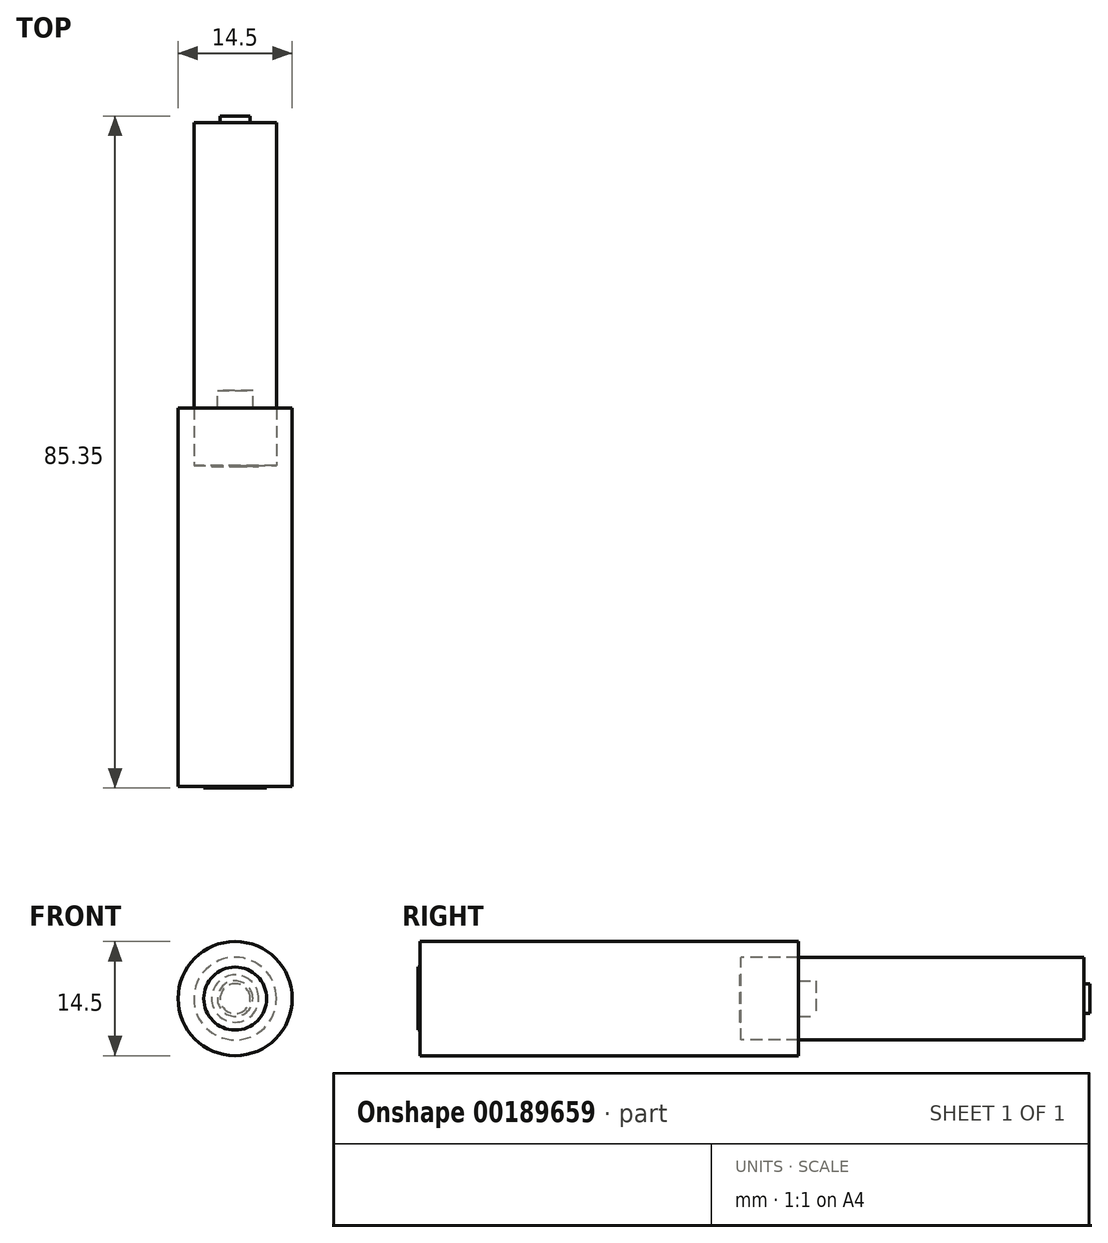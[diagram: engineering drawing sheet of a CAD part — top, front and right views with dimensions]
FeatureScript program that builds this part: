
annotation { "Feature Type Name" : "Feature", "Feature Type Description" : "" }
export const myFeature = defineFeature(function(context is Context, id is Id, definition is map)
    precondition{}
    {
        {
            var Q0;
            Q0=qCreatedBy(makeId("Top.planeOp"),FACE);
            var sketch = newSketch(context, id + "F0", { "sketchPlane" : qUnion([Q0])});
            skLineSegment(sketch, "E0", {"start": v(0, 47.95) * mm, "end": v(0, -12.14) * mm, "construction": true});
            skLineSegment(sketch, "E1", {"start": v(0, 0) * mm, "end": v(2.25, 0) * mm});
            skLineSegment(sketch, "E2", {"start": v(2.25, 0) * mm, "end": v(2.25, -2.2) * mm});
            skLineSegment(sketch, "E3", {"start": v(2.25, -2.2) * mm, "end": v(7.25, -2.2) * mm});
            skLineSegment(sketch, "E4", {"start": v(7.25, -2.2) * mm, "end": v(7.25, -50.3) * mm});
            skLineSegment(sketch, "E5", {"start": v(7.25, -50.3) * mm, "end": v(4, -50.3) * mm});
            skLineSegment(sketch, "E6", {"start": v(4, -50.3) * mm, "end": v(4, -50.5) * mm});
            skLineSegment(sketch, "E7", {"start": v(4, -50.5) * mm, "end": v(0, -50.5) * mm});
            skLineSegment(sketch, "E8", {"start": v(0, -50.5) * mm, "end": v(0, 0) * mm});
            skSolve(sketch);
        }
        {
            var Q0;
            Q0=qSketchRegion(id+"F0",true);
            var Q1;
            Q1=sQuery(id+"F0.wireOp",EDGE,"E0");
            revolve(context, id + "F1", {"entities" : qUnion([Q0]), "axis" : qUnion([Q1]), "revolveType" : RevolveType.FULL});
        }
        {
            var Q0;
            Q0=qCreatedBy(makeId("Top.planeOp"),FACE);
            var sketch = newSketch(context, id + "F2", { "sketchPlane" : qUnion([Q0])});
            skLineSegment(sketch, "E9", {"start": v(0, 34.85) * mm, "end": v(1.9, 34.85) * mm});
            skLineSegment(sketch, "E10", {"start": v(1.9, 34.85) * mm, "end": v(1.9, 34.05) * mm});
            skLineSegment(sketch, "E11", {"start": v(1.9, 34.05) * mm, "end": v(5.25, 34.05) * mm});
            skLineSegment(sketch, "E12", {"start": v(5.25, 34.05) * mm, "end": v(5.25, -9.5) * mm});
            skLineSegment(sketch, "E13", {"start": v(0, -9.65) * mm, "end": v(0, 34.85) * mm});
            skLineSegment(sketch, "E14", {"start": v(0, -9.65) * mm, "end": v(3, -9.65) * mm});
            skLineSegment(sketch, "E15", {"start": v(3, -9.65) * mm, "end": v(3, -9.5) * mm});
            skLineSegment(sketch, "E16", {"start": v(3, -9.5) * mm, "end": v(5.25, -9.5) * mm});
            skSolve(sketch);
        }
        {
            var Q0;
            Q0=qSketchRegion(id+"F2",true);
            var Q1;
            Q1=sQuery(id+"F2.wireOp",EDGE,"E13");
            revolve(context, id + "F3", {"entities" : qUnion([Q0]), "axis" : qUnion([Q1]), "revolveType" : RevolveType.FULL});
        }
    });
